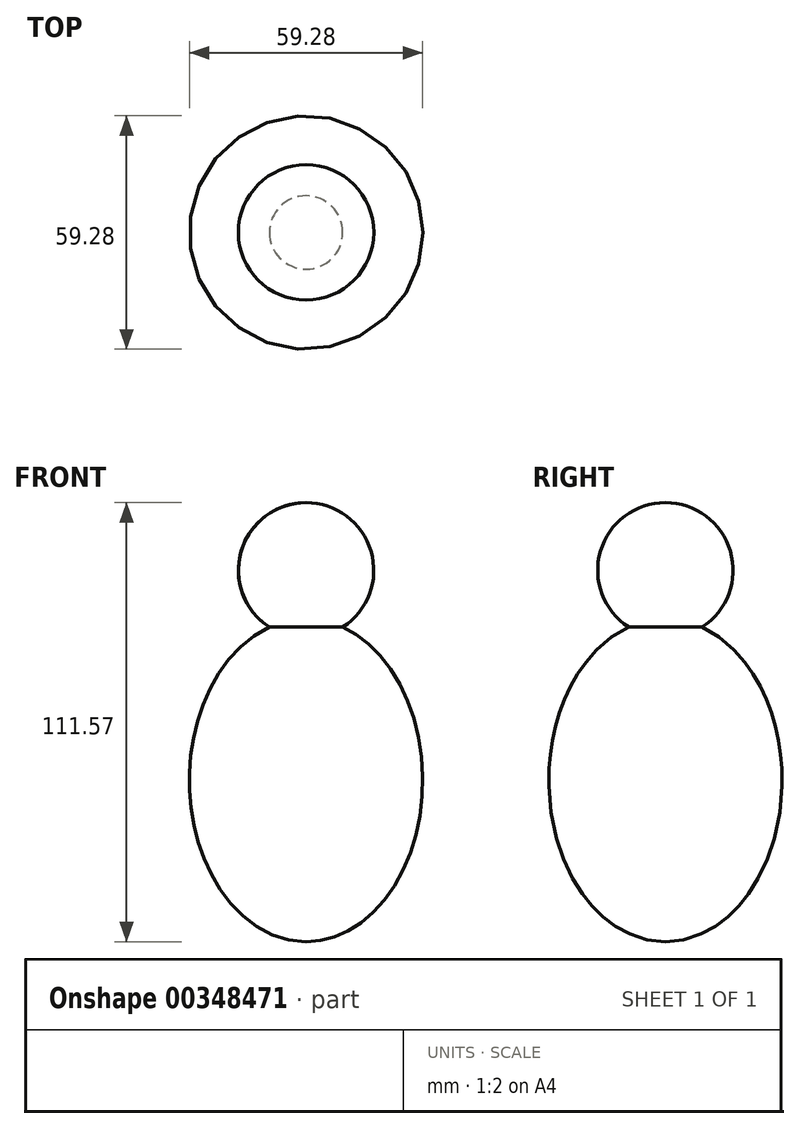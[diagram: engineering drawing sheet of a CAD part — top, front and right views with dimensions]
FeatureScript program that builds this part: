
annotation { "Feature Type Name" : "Feature", "Feature Type Description" : "" }
export const myFeature = defineFeature(function(context is Context, id is Id, definition is map)
    precondition{}
    {
        {
            var Q0;
            Q0=qCreatedBy(makeId("Front.planeOp"),FACE);
            var sketch = newSketch(context, id + "F0", { "sketchPlane" : qUnion([Q0])});
            skArc(sketch, "E0", {"start": v(0, 70.57) * mm, "mid": v(-17.2, 53.38) * mm, "end": v(0, 36.18) * mm});
            skLineSegment(sketch, "E1", {"start": v(0, 70.57) * mm, "end": v(0, 36.18) * mm});
            skPoint(sketch, "E2.orphan", {"position": v(0, 74.42) * mm});
            skSolve(sketch);
        }
        {
            var Q0;
            Q0=makeQuery(id+"F0.imprint","IMPRINT",FACE,{"disambiguationData":[TD([[makeQuery(id+"F0.imprint","IMPRINT",EDGE,{"derivedFrom":sQuery(id+"F0.wireOp",EDGE,"E0")}),1.0]])]});
            var Q1;
            Q1=sQuery(id+"F0.wireOp",EDGE,"E1");
            revolve(context, id + "F1", {"entities" : qUnion([Q0]), "axis" : qUnion([Q1]), "revolveType" : RevolveType.FULL});
        }
        {
            var Q0;
            Q0=qCreatedBy(makeId("Front.planeOp"),FACE);
            var sketch = newSketch(context, id + "F2", { "sketchPlane" : qUnion([Q0])});
            skEllipticalArc(sketch, "E3", {});
            skLineSegment(sketch, "E4", {"start": v(0, 41) * mm, "end": v(0, -41) * mm});
            const initialGuessF2  = {"E3": [0, 0, 0, 1, 0.040999509394168854, 0.029641795313543, 3.141592653589793, 0]};
            skSetInitialGuess(sketch, initialGuessF2);
            skSolve(sketch);
        }
        {
            var Q0;
            Q0=makeQuery(id+"F2.imprint","IMPRINT",FACE,{"disambiguationData":[TD([[makeQuery(id+"F2.imprint","IMPRINT",EDGE,{"derivedFrom":sQuery(id+"F2.wireOp",EDGE,"E3")}),1.0]])]});
            var Q1;
            Q1=sQuery(id+"F2.wireOp",EDGE,"E4");
            revolve(context, id + "F3", {"operationType" : NewBodyOperationType.ADD, "entities" : qUnion([Q0]), "axis" : qUnion([Q1]), "revolveType" : RevolveType.FULL});
        }
    });
